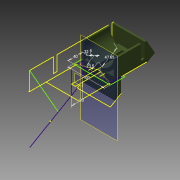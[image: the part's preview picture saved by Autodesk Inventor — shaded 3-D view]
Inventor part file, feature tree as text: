
AUTODESK INVENTOR PART (.ipt)
format: ipt  version: 2013 (Build 170138000, 138)  size: 288,256 bytes
history: native  units: mm
features: sketch x16, extrude x12, other x3
ambient origin geometry x8: Origin, YZ Plane, XZ Plane, XY Plane, X Axis, Y Axis, Z Axis, Center Point
feature tree (31):
  other  "ソリッド1"
  extrude  "押し出し1"  Depth=90.0mm
  extrude  "押し出し2"  Depth=50.0mm
  extrude  "押し出し3"  Depth=5.0mm
  extrude  "押し出し4"  Depth=85.0mm
  extrude  "押し出し6"  Depth=5.0mm
  sketch  "スケッチ9"
  extrude  "押し出し12"  Depth=80.0mm
  sketch  "スケッチ19"
  sketch  "スケッチ20"
  other  "作業平面5"
  extrude  "押し出し13"  Depth=10.0mm
  other  "作業平面6"
  extrude  "押し出し14"  Depth=90.0mm
  extrude  "押し出し15"  Depth=230.0mm TaperAngle=0.0deg
  sketch  "スケッチ24"
  sketch  "スケッチ25"
  extrude  "押し出し16"  Depth=225.0mm TaperAngle=0.0deg
  extrude  "押し出し17"  Depth=5.0mm TaperAngle=0.0deg
  extrude  "押し出し18"  Depth=65.0mm
  sketch  "スケッチ1"
  sketch  "スケッチ2"
  sketch  "スケッチ3"
  sketch  "スケッチ4"
  sketch  "スケッチ6"
  sketch  "スケッチ18"
  sketch  "スケッチ21"
  sketch  "スケッチ22"
  sketch  "スケッチ23"
  sketch  "スケッチ26"
  sketch  "スケッチ27"
